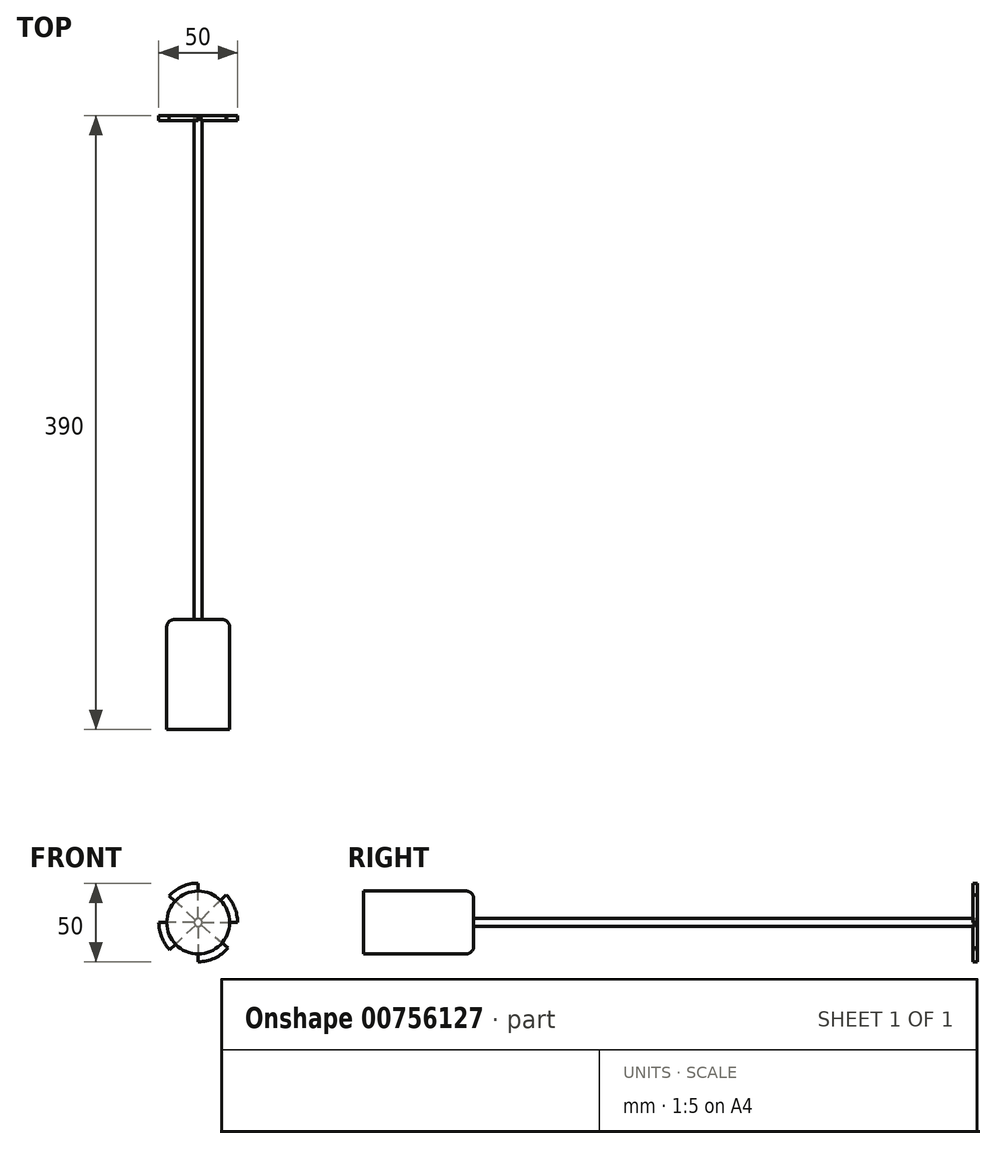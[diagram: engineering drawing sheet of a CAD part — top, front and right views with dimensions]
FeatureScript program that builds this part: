
annotation { "Feature Type Name" : "Feature", "Feature Type Description" : "" }
export const myFeature = defineFeature(function(context is Context, id is Id, definition is map)
    precondition{}
    {
        {
            var Q0;
            Q0=qCreatedBy(makeId("Front.planeOp"),FACE);
            var sketch = newSketch(context, id + "F0", { "sketchPlane" : qUnion([Q0])});
            skCircle(sketch, "E0", {"center": v(0, 0) * mm, "radius": 20 * mm});
            skSolve(sketch);
        }
        {
            var Q0;
            Q0=makeQuery(id+"F0.imprint","IMPRINT",FACE,{"disambiguationData":[TD([[makeQuery(id+"F0.imprint","IMPRINT",EDGE,{"derivedFrom":sQuery(id+"F0.wireOp",EDGE,"E0")}),1.0]])]});
            extrude(context, id + "F1", {"entities" : qUnion([Q0]), "depth" : 70 * mm, "offsetDistance" : 25 * mm});
        }
        {
            var Q0;
            Q0=makeQuery(id+"F1.opExtrude","CAP_FACE",FACE,{"disambiguationData":[OSD([sQuery(id+"F0.wireOp",EDGE,"E0")])],"isStart":true});
            var sketch = newSketch(context, id + "F2", { "sketchPlane" : qUnion([Q0])});
            skCircle(sketch, "E1", {"center": v(0, 0) * mm, "radius": 2.5 * mm});
            skSolve(sketch);
        }
        {
            var Q0;
            Q0=makeQuery(id+"F2.imprint","IMPRINT",FACE,{"disambiguationData":[TD([[makeQuery(id+"F2.imprint","IMPRINT",EDGE,{"derivedFrom":sQuery(id+"F2.wireOp",EDGE,"E1")}),1.0]])]});
            extrude(context, id + "F3", {"entities" : qUnion([Q0]), "operationType" : NewBodyOperationType.ADD, "depth" : 320 * mm, "offsetDistance" : 25 * mm});
        }
        {
            var Q0;
            Q0=makeQuery(id+"F3.opExtrude","CAP_FACE",FACE,{"disambiguationData":[OSD([sQuery(id+"F2.wireOp",EDGE,"E1")])],"isStart":false});
            var sketch = newSketch(context, id + "F4", { "sketchPlane" : qUnion([Q0])});
            skCircle(sketch, "E2", {"center": v(0, 0) * mm, "radius": 25 * mm});
            skLineSegment(sketch, "E3", {"start": v(0, 0) * mm, "end": v(0, 25) * mm});
            skLineSegment(sketch, "E4", {"start": v(0, 0) * mm, "end": v(0, -25) * mm});
            skLineSegment(sketch, "E5", {"start": v(0, 0) * mm, "end": v(25, 0) * mm});
            skLineSegment(sketch, "E6", {"start": v(0, 0) * mm, "end": v(-25, 0) * mm});
            skLineSegment(sketch, "E7", {"start": v(0, 0) * mm, "end": v(-17.66, 17.7) * mm});
            skLineSegment(sketch, "E8", {"start": v(0, 0) * mm, "end": v(18.11, -17.23) * mm});
            skLineSegment(sketch, "E9", {"start": v(0, 0) * mm, "end": v(18.4, 16.92) * mm});
            skLineSegment(sketch, "E10", {"start": v(0, 0) * mm, "end": v(-19.07, -16.16) * mm});
            skSolve(sketch);
        }
        {
            var Q0;
            {var subQ0=sQuery(id+"F4.wireOp",EDGE,"E3");var subQ1=sQuery(id+"F4.wireOp",EDGE,"E2");var subQ2=makeQuery(id+"F4.imprint","INTERSECT",VERTEX,{"derivedFrom":[subQ1,subQ0]});Q0=makeQuery(id+"F4.imprint","IMPRINT",FACE,{"disambiguationData":[TD([[makeQuery(id+"F4.imprint","IMPRINT",EDGE,{"disambiguationData":[TD([[subQ2,1.0]])],"derivedFrom":subQ1}),1.0]])]});}
            var Q1;
            {var subQ0=sQuery(id+"F4.wireOp",EDGE,"E5");var subQ1=sQuery(id+"F4.wireOp",EDGE,"E2");var subQ2=makeQuery(id+"F4.imprint","INTERSECT",VERTEX,{"derivedFrom":[subQ1,subQ0]});Q1=makeQuery(id+"F4.imprint","IMPRINT",FACE,{"disambiguationData":[TD([[makeQuery(id+"F4.imprint","IMPRINT",EDGE,{"disambiguationData":[TD([[subQ2,1.0]])],"derivedFrom":subQ1}),1.0]])]});}
            var Q2;
            {var subQ0=sQuery(id+"F4.wireOp",EDGE,"E4");var subQ1=sQuery(id+"F4.wireOp",EDGE,"E2");var subQ2=makeQuery(id+"F4.imprint","INTERSECT",VERTEX,{"derivedFrom":[subQ1,subQ0]});Q2=makeQuery(id+"F4.imprint","IMPRINT",FACE,{"disambiguationData":[TD([[makeQuery(id+"F4.imprint","IMPRINT",EDGE,{"disambiguationData":[TD([[subQ2,1.0]])],"derivedFrom":subQ1}),1.0]])]});}
            var Q3;
            {var subQ0=sQuery(id+"F4.wireOp",EDGE,"E6");var subQ1=sQuery(id+"F4.wireOp",EDGE,"E2");var subQ2=makeQuery(id+"F4.imprint","INTERSECT",VERTEX,{"derivedFrom":[subQ1,subQ0]});Q3=makeQuery(id+"F4.imprint","IMPRINT",FACE,{"disambiguationData":[TD([[makeQuery(id+"F4.imprint","IMPRINT",EDGE,{"disambiguationData":[TD([[subQ2,1.0]])],"derivedFrom":subQ1}),1.0]])]});}
            extrude(context, id + "F5", {"entities" : qUnion([Q0, Q1, Q2, Q3]), "operationType" : NewBodyOperationType.ADD, "oppositeDirection" : true, "depth" : 3 * mm, "offsetDistance" : 25 * mm});
        }
        {
            var Q0;
            Q0=makeQuery(id+"F1.opExtrude","CAP_EDGE",EDGE,{"disambiguationData":[OSD([sQuery(id+"F0.wireOp",EDGE,"E0")])],"isStart":true});
            fillet(context, id + "F6", {"entities" : qUnion([Q0]), "tangentPropagation" : true, "radius" : 5 * mm, "defaultsChanged" : false, "vertexSettings" : [], "allowEdgeOverflow" : false});
        }
    });
